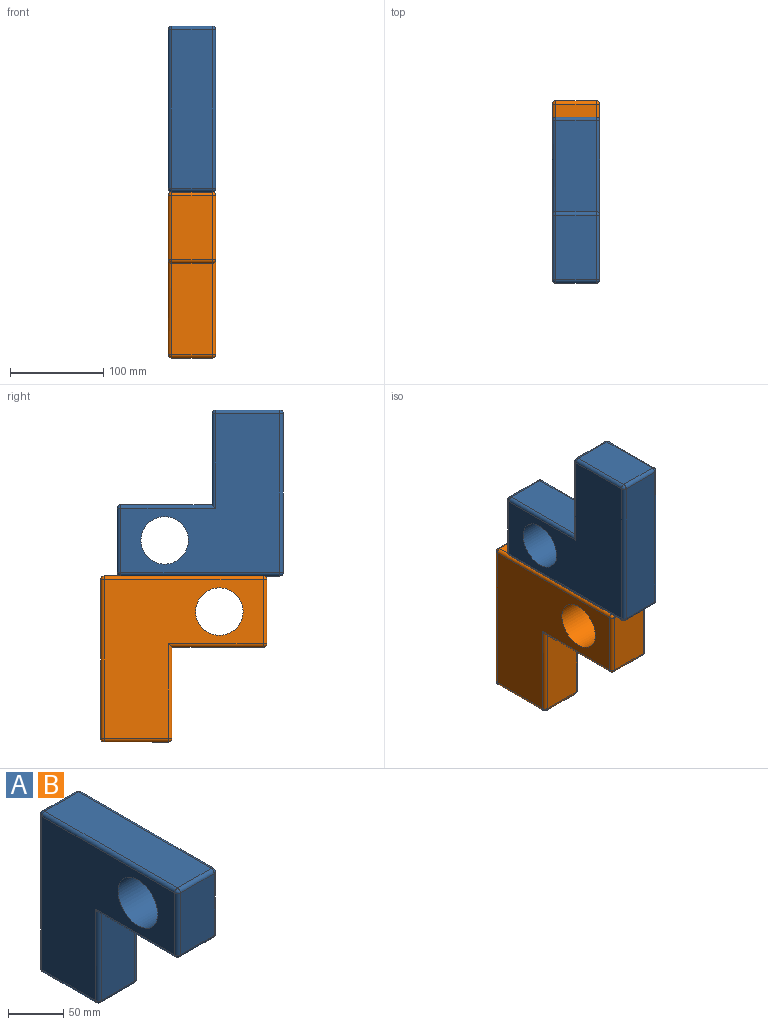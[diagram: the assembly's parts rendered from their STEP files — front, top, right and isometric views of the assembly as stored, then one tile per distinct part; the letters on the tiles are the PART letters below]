
ASSEMBLY  parts=2 mates=2
PART A: 36 faces, bbox 50.8x177.8x177.8 mm
  f0: plane 68.58x43.18mm, normal (0,-1,0), area 2961.3mm2, adj f24,f29,f32,f35
  f1: plane 97.79x43.18mm, normal (0,0,-1), area 4222.6mm2, adj f2,f30,f31,f35
  f2: plane 97.79x43.18mm, normal (0,-1,0), area 4222.6mm2, adj f1,f17,f26,f27
  f3: plane 68.58x43.18mm, normal (0,0,-1), area 2961.3mm2, adj f9,f16,f17,f18
  f4: plane 170.18x43.18mm, normal (0,1,0), area 7348.4mm2, adj f9,f10,f13,f14
  f5: plane 170.18x43.18mm, normal (0,0,1), area 7348.4mm2, adj f14,f20,f23,f24
  f6: plane 170.18x170.18mm, normal (1,0,0), area 16611.8mm2, adj f8,f10,f16,f20,f26,f29,f30
  f7: plane 170.18x170.18mm, normal (-1,0,0), area 16611.8mm2, adj f8,f13,f18,f23,f27,f31,f32
  f8: cylinder r=25.4mm len=50.8mm, axis (1,0,0), area 8107.3mm2, adj f6,f7
  f9: cylinder r=3.81mm len=43.18mm, axis (-1,0,0), area 258.4mm2, adj f3,f4,f11,f12
  f10: cylinder r=3.81mm len=170.18mm, axis (0,0,-1), area 1018.5mm2, adj f4,f6,f11,f15
  f11: sphere r=3.81mm, area 22.8mm2, adj f9,f10,f16
  f12: sphere r=3.81mm, area 22.8mm2, adj f9,f13,f18
  f13: cylinder r=3.81mm len=170.18mm, axis (0,0,1), area 1018.5mm2, adj f4,f7,f12,f19
  f14: cylinder r=3.81mm len=43.18mm, axis (-1,0,0), area 258.4mm2, adj f4,f5,f15,f19
  f15: sphere r=3.81mm, area 22.8mm2, adj f10,f14,f20
  f16: cylinder r=3.81mm len=68.58mm, axis (0,-1,0), area 410.4mm2, adj f3,f6,f11,f21
  f17: cylinder r=3.81mm len=43.18mm, axis (-1,0,0), area 258.4mm2, adj f2,f3,f21,f22
  f18: cylinder r=3.81mm len=68.58mm, axis (0,1,0), area 410.4mm2, adj f3,f7,f12,f22
  f19: sphere r=3.81mm, area 22.8mm2, adj f13,f14,f23
  f20: cylinder r=3.81mm len=170.18mm, axis (0,1,0), area 1018.5mm2, adj f5,f6,f15,f25
  f21: sphere r=3.81mm, area 22.8mm2, adj f16,f17,f26
  f22: sphere r=3.81mm, area 22.8mm2, adj f17,f18,f27
  f23: cylinder r=3.81mm len=170.18mm, axis (0,-1,0), area 1018.5mm2, adj f5,f7,f19,f28
  f24: cylinder r=3.81mm len=43.18mm, axis (-1,0,0), area 258.4mm2, adj f0,f5,f25,f28
  f25: sphere r=3.81mm, area 22.8mm2, adj f20,f24,f29
  f26: cylinder r=3.81mm len=101.6mm, axis (0,0,1), area 593.5mm2, adj f2,f6,f21,f30
  f27: cylinder r=3.81mm len=101.6mm, axis (0,0,-1), area 593.5mm2, adj f2,f7,f22,f31
  f28: sphere r=3.81mm, area 22.8mm2, adj f23,f24,f32
  f29: cylinder r=3.81mm len=68.58mm, axis (0,0,1), area 410.4mm2, adj f0,f6,f25,f33
  f30: cylinder r=3.81mm len=101.6mm, axis (0,-1,0), area 593.5mm2, adj f1,f6,f26,f33
  f31: cylinder r=3.81mm len=101.6mm, axis (0,1,0), area 593.5mm2, adj f1,f7,f27,f34
  f32: cylinder r=3.81mm len=68.58mm, axis (0,0,-1), area 410.4mm2, adj f0,f7,f28,f34
  f33: sphere r=3.81mm, area 22.8mm2, adj f29,f30,f35
  f34: sphere r=3.81mm, area 22.8mm2, adj f31,f32,f35
  f35: cylinder r=3.81mm len=43.18mm, axis (-1,0,0), area 258.4mm2, adj f0,f1,f33,f34
PART B: same geometry as A
PLACE A rot(axis=(-1,0,0),180deg) t=(-138.62,-0.7,-111.75)mm
PLACE B t=(-138.62,42.27,-264.15)mm
MATE planar B.f5 <-> A.f5  axis (0,0,1) through (-113.22,29.57,-187.95)mm
MATE planar A.f6 <-> B.f6  axis (1,0,0) through (-87.82,-13.96,-114.16)mm
